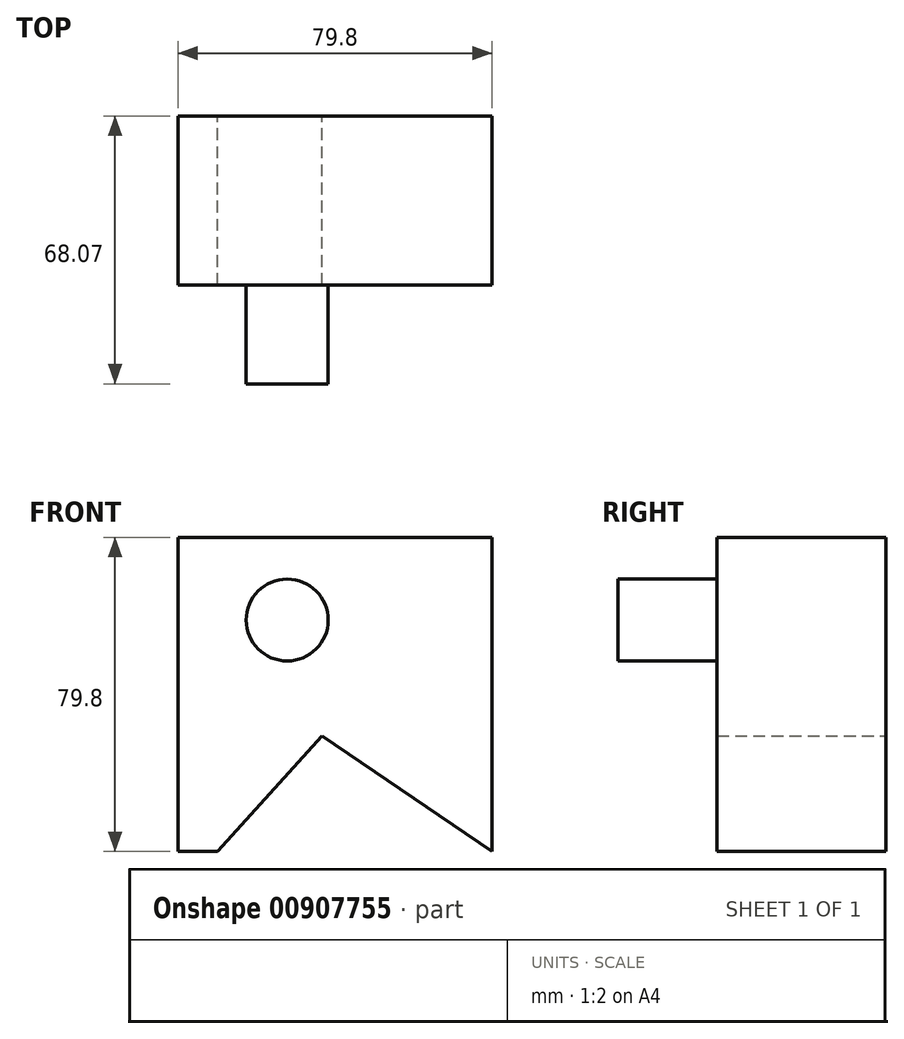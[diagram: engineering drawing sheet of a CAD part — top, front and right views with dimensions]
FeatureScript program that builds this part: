
annotation { "Feature Type Name" : "Feature", "Feature Type Description" : "" }
export const myFeature = defineFeature(function(context is Context, id is Id, definition is map)
    precondition{}
    {
        {
            var Q0;
            Q0=qCreatedBy(makeId("Front.planeOp"),FACE);
            var sketch = newSketch(context, id + "F0", { "sketchPlane" : qUnion([Q0])});
            skLineSegment(sketch, "E0", {"start": v(-43.05, 34.02) * mm, "end": v(-43.05, -45.78) * mm});
            skLineSegment(sketch, "E1", {"start": v(36.75, -45.78) * mm, "end": v(36.75, 34.02) * mm});
            skLineSegment(sketch, "E2", {"start": v(36.75, 34.02) * mm, "end": v(-43.05, 34.02) * mm});
            skLineSegment(sketch, "E3", {"start": v(-32.97, -45.78) * mm, "end": v(-6.5, -16.38) * mm});
            skLineSegment(sketch, "E4", {"start": v(-6.5, -16.38) * mm, "end": v(36.75, -45.78) * mm});
            skLineSegment(sketch, "E5", {"start": v(-43.05, -45.78) * mm, "end": v(-32.97, -45.78) * mm});
            skSolve(sketch);
        }
        {
            var Q0;
            Q0=makeQuery(id+"F0.imprint","IMPRINT",FACE,{"disambiguationData":[TD([[makeQuery(id+"F0.imprint","IMPRINT",EDGE,{"derivedFrom":sQuery(id+"F0.wireOp",EDGE,"E0")}),1.0]])]});
            extrude(context, id + "F1", {"entities" : qUnion([Q0]), "depth" : 42.93 * mm, "offsetDistance" : 25.4 * mm});
        }
        {
            var Q0;
            Q0=qCreatedBy(makeId("Front.planeOp"),FACE);
            var sketch = newSketch(context, id + "F2", { "sketchPlane" : qUnion([Q0])});
            skCircle(sketch, "E6", {"center": v(-15.33, 13.02) * mm, "radius": 10.4 * mm});
            skSolve(sketch);
        }
        {
            var Q0;
            Q0=makeQuery(id+"F2.imprint","IMPRINT",FACE,{"disambiguationData":[TD([[makeQuery(id+"F2.imprint","IMPRINT",EDGE,{"derivedFrom":sQuery(id+"F2.wireOp",EDGE,"E6")}),1.0]])]});
            extrude(context, id + "F3", {"entities" : qUnion([Q0]), "operationType" : NewBodyOperationType.ADD, "depth" : 68.07 * mm, "offsetDistance" : 25.4 * mm});
        }
    });
